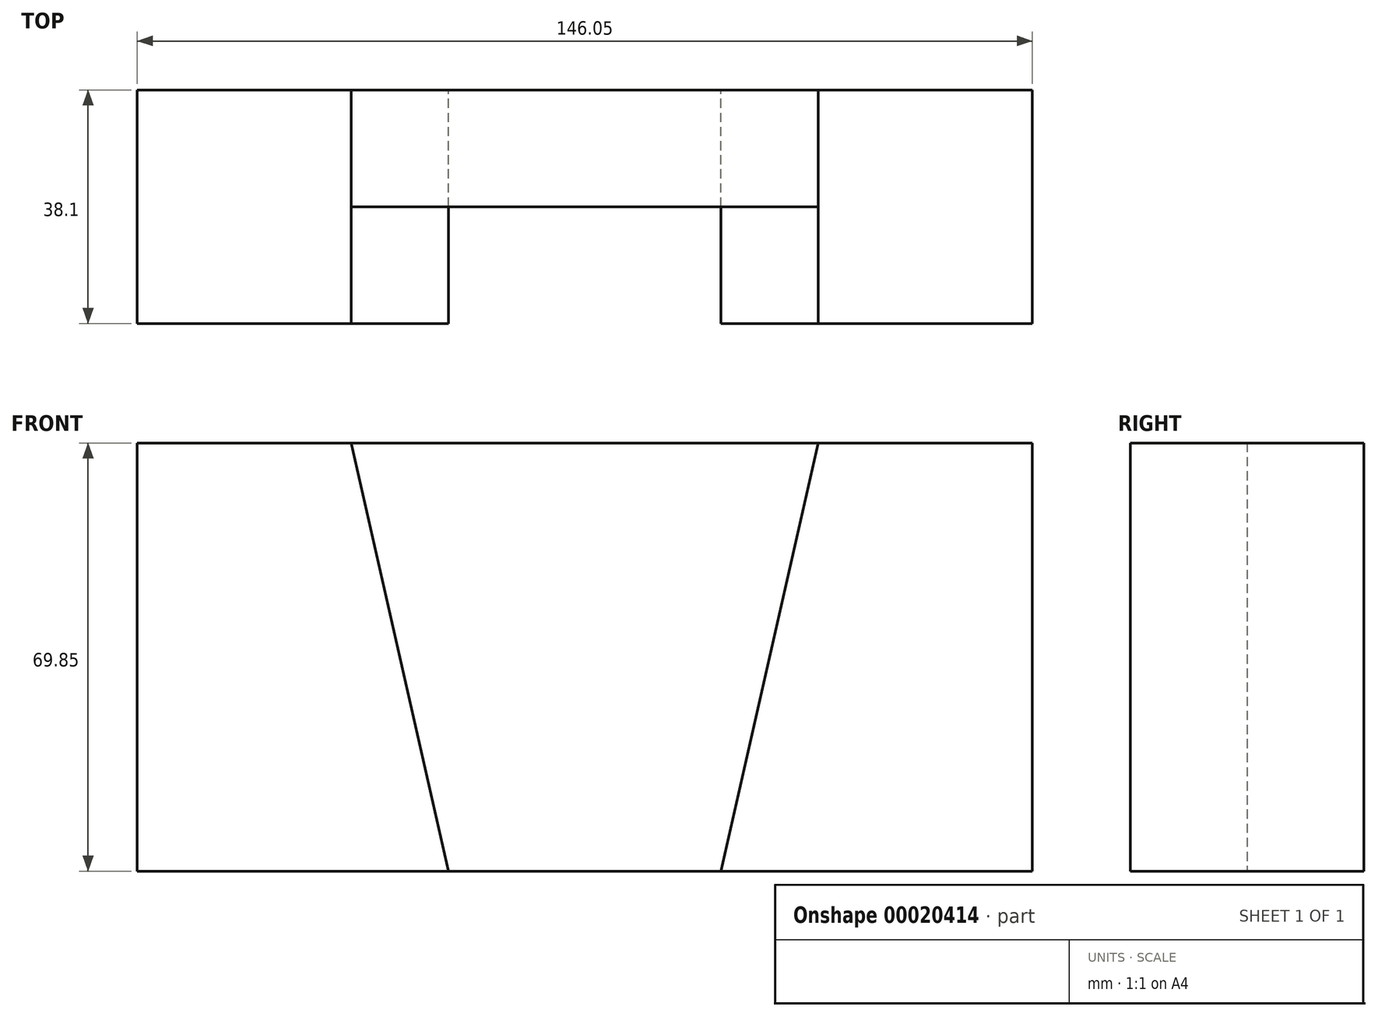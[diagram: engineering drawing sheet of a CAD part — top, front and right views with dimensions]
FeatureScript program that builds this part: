
annotation { "Feature Type Name" : "Feature", "Feature Type Description" : "" }
export const myFeature = defineFeature(function(context is Context, id is Id, definition is map)
    precondition{}
    {
        {
            var Q0;
            Q0=qCreatedBy(makeId("Front.planeOp"),FACE);
            var sketch = newSketch(context, id + "F0", { "sketchPlane" : qUnion([Q0])});
            skLineSegment(sketch, "E0", {"start": v(-55.2, 40.4) * mm, "end": v(90.85, 40.4) * mm});
            skLineSegment(sketch, "E1", {"start": v(90.85, 40.4) * mm, "end": v(90.85, -29.45) * mm});
            skLineSegment(sketch, "E2", {"start": v(90.85, -29.45) * mm, "end": v(-55.2, -29.45) * mm});
            skLineSegment(sketch, "E3", {"start": v(-55.2, -29.45) * mm, "end": v(-55.2, 40.4) * mm});
            skLineSegment(sketch, "E4", {"start": v(55.92, 40.4) * mm, "end": v(40.05, -29.45) * mm});
            skLineSegment(sketch, "E5", {"start": v(-20.28, 40.4) * mm, "end": v(-4.4, -29.45) * mm});
            skSolve(sketch);
        }
        {
            var Q0;
            {var subQ2=sQuery(id+"F0.wireOp",EDGE,"E3");Q0=makeQuery(id+"F0.imprint","IMPRINT",FACE,{"disambiguationData":[TD([[makeQuery(id+"F0.imprint","IMPRINT",EDGE,{"derivedFrom":subQ2}),-1.0]])]});}
            var Q1;
            {var subQ2=sQuery(id+"F0.wireOp",EDGE,"E1");Q1=makeQuery(id+"F0.imprint","IMPRINT",FACE,{"disambiguationData":[TD([[makeQuery(id+"F0.imprint","IMPRINT",EDGE,{"derivedFrom":subQ2}),-1.0]])]});}
            extrude(context, id + "F1", {"entities" : qUnion([Q0, Q1]), "depth" : 38.1 * mm});
        }
        {
            var Q0;
            {var subQ1=sQuery(id+"F0.wireOp",EDGE,"E4");Q0=makeQuery(id+"F0.imprint","IMPRINT",FACE,{"disambiguationData":[TD([[makeQuery(id+"F0.imprint","IMPRINT",EDGE,{"derivedFrom":subQ1}),-1.0]])]});}
            extrude(context, id + "F2", {"entities" : qUnion([Q0]), "depth" : 19.05 * mm});
        }
    });
